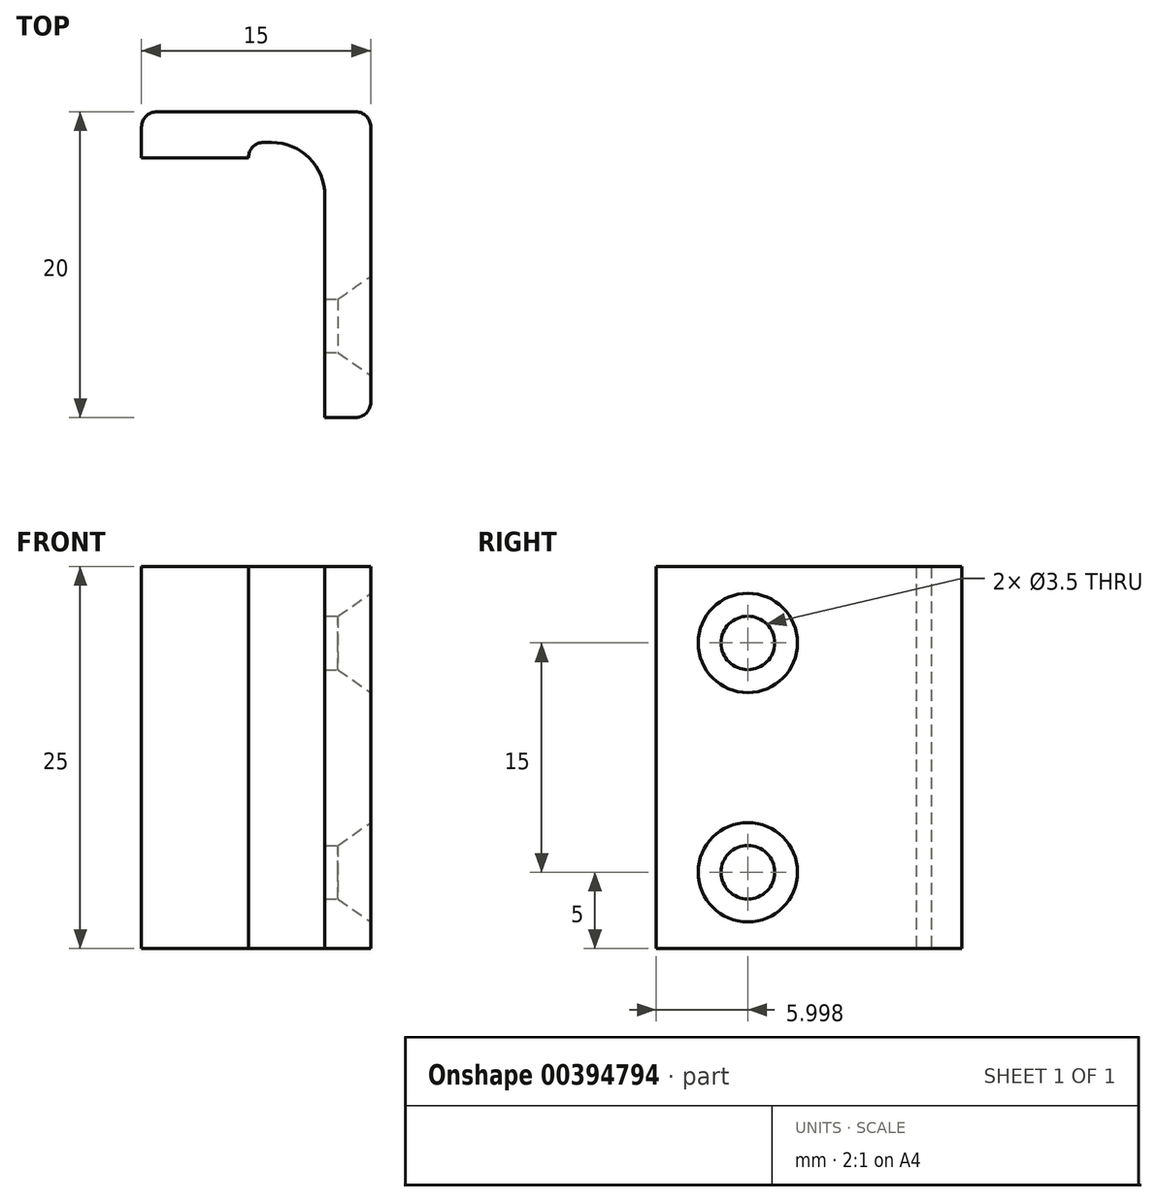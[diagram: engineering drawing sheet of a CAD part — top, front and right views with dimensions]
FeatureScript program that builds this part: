
annotation { "Feature Type Name" : "Feature", "Feature Type Description" : "" }
export const myFeature = defineFeature(function(context is Context, id is Id, definition is map)
    precondition{}
    {
        {
            var Q0;
            Q0=qCreatedBy(makeId("Top.planeOp"),FACE);
            var sketch = newSketch(context, id + "F0", { "sketchPlane" : qUnion([Q0])});
            skLineSegment(sketch, "E0", {"start": v(-8.53, -11.78) * mm, "end": v(4.47, -11.78) * mm});
            skLineSegment(sketch, "E1", {"start": v(5.47, -12.78) * mm, "end": v(5.47, -30.78) * mm});
            skLineSegment(sketch, "E2", {"start": v(4.47, -31.78) * mm, "end": v(2.47, -31.78) * mm});
            skLineSegment(sketch, "E3", {"start": v(2.47, -31.78) * mm, "end": v(2.47, -17.28) * mm});
            skLineSegment(sketch, "E4", {"start": v(-1.03, -13.78) * mm, "end": v(-1.53, -13.78) * mm});
            skLineSegment(sketch, "E5", {"start": v(-2.53, -14.78) * mm, "end": v(-2.53, -14.78) * mm});
            skLineSegment(sketch, "E6", {"start": v(-2.53, -14.78) * mm, "end": v(-9.53, -14.78) * mm});
            skLineSegment(sketch, "E7", {"start": v(-9.53, -14.78) * mm, "end": v(-9.53, -12.78) * mm});
            skPoint(sketch, "E8.visualSharp", {"position": v(2.47, -13.78) * mm});
            skArc(sketch, "E8.filletArc", {"start": v(2.47, -17.28) * mm, "mid": v(1.45, -14.8) * mm, "end": v(-1.03, -13.78) * mm});
            skPoint(sketch, "E9.visualSharp", {"position": v(-2.53, -13.78) * mm});
            skArc(sketch, "E9.filletArc", {"start": v(-1.53, -13.78) * mm, "mid": v(-2.23, -14.08) * mm, "end": v(-2.53, -14.78) * mm});
            skPoint(sketch, "E10.visualSharp", {"position": v(-9.53, -11.78) * mm});
            skArc(sketch, "E10.filletArc", {"start": v(-8.53, -11.78) * mm, "mid": v(-9.23, -12.08) * mm, "end": v(-9.53, -12.78) * mm});
            skPoint(sketch, "E11.visualSharp", {"position": v(5.47, -11.78) * mm});
            skArc(sketch, "E11.filletArc", {"start": v(5.47, -12.78) * mm, "mid": v(5.18, -12.08) * mm, "end": v(4.47, -11.78) * mm});
            skPoint(sketch, "E12.visualSharp", {"position": v(5.47, -31.78) * mm});
            skArc(sketch, "E12.filletArc", {"start": v(4.47, -31.78) * mm, "mid": v(5.18, -31.49) * mm, "end": v(5.47, -30.78) * mm});
            skSolve(sketch);
        }
        {
            var Q0;
            Q0=makeQuery(id+"F0.imprint","IMPRINT",FACE,{"disambiguationData":[TD([[makeQuery(id+"F0.imprint","IMPRINT",EDGE,{"derivedFrom":sQuery(id+"F0.wireOp",EDGE,"E0")}),-1.0]])]});
            extrude(context, id + "F1", {"entities" : qUnion([Q0]), "depth" : 25 * mm});
        }
        {
            var Q0;
            Q0=makeQuery(id+"F1.opExtrude","SWEPT_FACE",FACE,{"disambiguationData":[OSD([sQuery(id+"F0.wireOp",EDGE,"E1")])]});
            var sketch = newSketch(context, id + "F2", { "sketchPlane" : qUnion([Q0])});
            skPoint(sketch, "E13", {"position": v(-25.78, 20) * mm});
            skPoint(sketch, "E14", {"position": v(-25.78, 5) * mm});
            skSolve(sketch);
        }
        {
            var Q0;
            Q0=sQuery(id+"F2.wireOp",VERTEX,"E13");
            var Q1;
            Q1=sQuery(id+"F2.wireOp",VERTEX,"E14");
            var Q2;
            Q2=makeQuery(id+"F1.opExtrude","SWEPT_BODY",BODY,{"disambiguationData":[OSD([sQuery(id+"F0.wireOp",EDGE,"E0"),sQuery(id+"F0.wireOp",EDGE,"E1"),sQuery(id+"F0.wireOp",EDGE,"E2"),sQuery(id+"F0.wireOp",EDGE,"E3"),sQuery(id+"F0.wireOp",EDGE,"E4"),sQuery(id+"F0.wireOp",EDGE,"E6"),sQuery(id+"F0.wireOp",EDGE,"E7"),sQuery(id+"F0.wireOp",EDGE,"E8.filletArc"),sQuery(id+"F0.wireOp",EDGE,"E9.filletArc"),sQuery(id+"F0.wireOp",EDGE,"E10.filletArc"),sQuery(id+"F0.wireOp",EDGE,"E11.filletArc"),sQuery(id+"F0.wireOp",EDGE,"E12.filletArc")])]});
            hole(context, id + "F3", {"style" : HoleStyle.C_SINK, "endStyle" : HoleEndStyle.THROUGH, "holeDiameter" : 3.5 * mm, "cSinkDiameter" : 6.5 * mm, "cSinkAngle" : 70 * degree, "tappedDepth" : 12 * mm, "tapClearance" : 3, "startFromSketch" : true, "locations" : qUnion([Q0, Q1]), "scope" : qUnion([Q2])});
        }
    });
